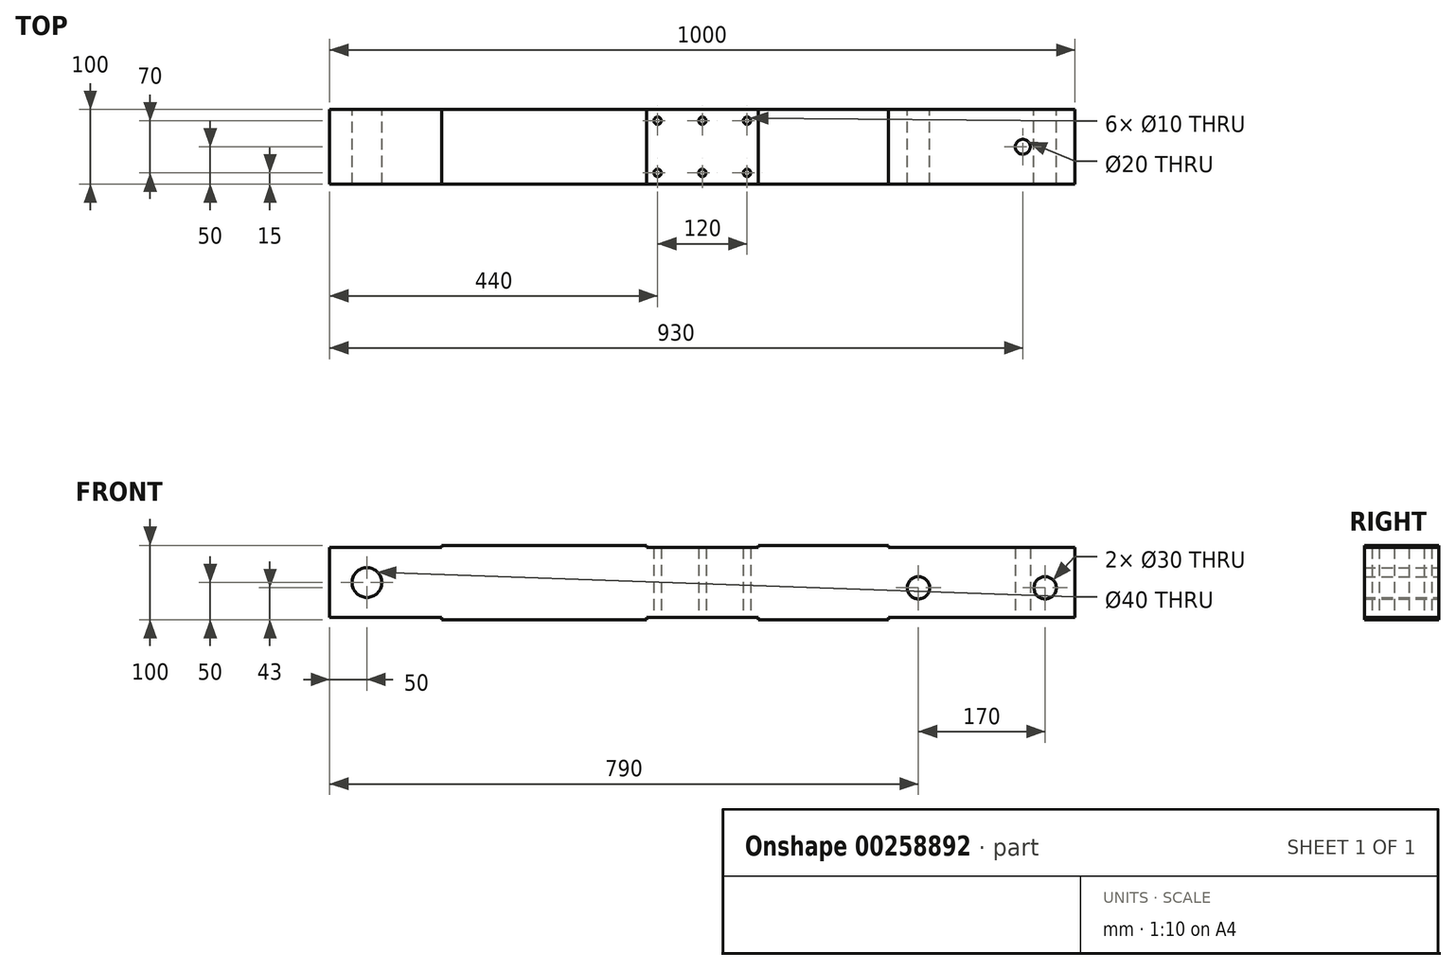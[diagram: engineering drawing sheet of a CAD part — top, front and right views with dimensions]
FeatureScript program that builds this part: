
annotation { "Feature Type Name" : "Feature", "Feature Type Description" : "" }
export const myFeature = defineFeature(function(context is Context, id is Id, definition is map)
    precondition{}
    {
        {
            var Q0;
            Q0=qCreatedBy(makeId("Top.planeOp"),FACE);
            var sketch = newSketch(context, id + "F0", { "sketchPlane" : qUnion([Q0])});
            skLineSegment(sketch, "E0.bottom", {"start": v(-75, 50) * mm, "end": v(75, 50) * mm});
            skLineSegment(sketch, "E0.top", {"start": v(-75, -50) * mm, "end": v(75, -50) * mm});
            skLineSegment(sketch, "E0.left", {"start": v(-75, 50) * mm, "end": v(-75, -50) * mm, "construction": true});
            skLineSegment(sketch, "E0.right", {"start": v(75, 50) * mm, "end": v(75, -50) * mm, "construction": true});
            skPoint(sketch, "E0.middle", {"position": v(0, 0) * mm});
            skLineSegment(sketch, "E1.bottom", {"start": v(-500, 50) * mm, "end": v(500, 50) * mm});
            skLineSegment(sketch, "E1.top", {"start": v(-500, -50) * mm, "end": v(500, -50) * mm});
            skLineSegment(sketch, "E1.left", {"start": v(-500, 50) * mm, "end": v(-500, -50) * mm});
            skLineSegment(sketch, "E1.right", {"start": v(500, 50) * mm, "end": v(500, -50) * mm});
            skLineSegment(sketch, "E2.bottom", {"start": v(-60, 35) * mm, "end": v(60, 35) * mm, "construction": true});
            skLineSegment(sketch, "E2.top", {"start": v(-60, -35) * mm, "end": v(60, -35) * mm, "construction": true});
            skLineSegment(sketch, "E2.left", {"start": v(-60, 35) * mm, "end": v(-60, -35) * mm, "construction": true});
            skLineSegment(sketch, "E2.right", {"start": v(60, 35) * mm, "end": v(60, -35) * mm, "construction": true});
            skCircle(sketch, "E3", {"center": v(-60, 35) * mm, "radius": 5 * mm});
            skCircle(sketch, "E4", {"center": v(-60, -35) * mm, "radius": 5 * mm});
            skCircle(sketch, "E5", {"center": v(0, -35) * mm, "radius": 5 * mm});
            skCircle(sketch, "E6", {"center": v(60, -35) * mm, "radius": 5 * mm});
            skCircle(sketch, "E7", {"center": v(60, 35) * mm, "radius": 5 * mm});
            skCircle(sketch, "E8", {"center": v(0, 35) * mm, "radius": 5 * mm});
            skLineSegment(sketch, "E9", {"start": v(430, 50) * mm, "end": v(430, 0) * mm, "construction": true});
            skLineSegment(sketch, "E10", {"start": v(430, 0) * mm, "end": v(430, -50) * mm, "construction": true});
            skLineSegment(sketch, "E11", {"start": v(430, 0) * mm, "end": v(500, 0) * mm, "construction": true});
            skCircle(sketch, "E12", {"center": v(430, 0) * mm, "radius": 10 * mm});
            skSolve(sketch);
        }
        {
            var Q0;
            Q0=qCreatedBy(makeId("Front.planeOp"),FACE);
            var sketch = newSketch(context, id + "F1", { "sketchPlane" : qUnion([Q0])});
            skLineSegment(sketch, "E13.bottom", {"start": v(-75, 47) * mm, "end": v(75, 47) * mm});
            skLineSegment(sketch, "E13.top", {"start": v(-75, -47) * mm, "end": v(75, -47) * mm});
            skLineSegment(sketch, "E13.left", {"start": v(-75, 47) * mm, "end": v(-75, -47) * mm, "construction": true});
            skLineSegment(sketch, "E13.right", {"start": v(75, 47) * mm, "end": v(75, -47) * mm, "construction": true});
            skPoint(sketch, "E13.middle", {"position": v(0, 0) * mm});
            skLineSegment(sketch, "E14", {"start": v(-75, 47) * mm, "end": v(-75, 50) * mm});
            skLineSegment(sketch, "E15", {"start": v(-75, 50) * mm, "end": v(-350, 50) * mm});
            skLineSegment(sketch, "E16", {"start": v(-350, -50) * mm, "end": v(-75, -50) * mm});
            skLineSegment(sketch, "E17", {"start": v(-75, -50) * mm, "end": v(-75, -47) * mm});
            skLineSegment(sketch, "E18", {"start": v(75, -47) * mm, "end": v(75, -50) * mm});
            skLineSegment(sketch, "E19", {"start": v(75, -50) * mm, "end": v(250, -50) * mm});
            skLineSegment(sketch, "E20", {"start": v(250, 50) * mm, "end": v(75, 50) * mm});
            skLineSegment(sketch, "E21", {"start": v(75, 50) * mm, "end": v(75, 47) * mm});
            skLineSegment(sketch, "E22", {"start": v(250, 50) * mm, "end": v(250, 47) * mm});
            skLineSegment(sketch, "E23", {"start": v(250, 47) * mm, "end": v(250, -47) * mm, "construction": true});
            skLineSegment(sketch, "E24", {"start": v(250, -47) * mm, "end": v(250, -50) * mm});
            skLineSegment(sketch, "E25", {"start": v(-350, 50) * mm, "end": v(-350, 47) * mm});
            skLineSegment(sketch, "E26", {"start": v(-350, 47) * mm, "end": v(-350, -47) * mm, "construction": true});
            skLineSegment(sketch, "E27", {"start": v(-350, -47) * mm, "end": v(-350, -50) * mm});
            skLineSegment(sketch, "E28", {"start": v(-350, 47) * mm, "end": v(-500, 47) * mm});
            skLineSegment(sketch, "E29", {"start": v(-500, 47) * mm, "end": v(-500, -47) * mm});
            skLineSegment(sketch, "E30", {"start": v(-500, -47) * mm, "end": v(-350, -47) * mm});
            skLineSegment(sketch, "E31", {"start": v(250, 47) * mm, "end": v(500, 47) * mm});
            skLineSegment(sketch, "E32", {"start": v(500, 47) * mm, "end": v(500, -47) * mm});
            skLineSegment(sketch, "E33", {"start": v(500, -47) * mm, "end": v(250, -47) * mm});
            skLineSegment(sketch, "E34", {"start": v(250, 33) * mm, "end": v(500, 33) * mm, "construction": true});
            skLineSegment(sketch, "E35", {"start": v(290, 33) * mm, "end": v(290, -7) * mm, "construction": true});
            skLineSegment(sketch, "E36", {"start": v(290, -7) * mm, "end": v(250, -7) * mm, "construction": true});
            skLineSegment(sketch, "E37", {"start": v(290, -7) * mm, "end": v(290, -47) * mm, "construction": true});
            skLineSegment(sketch, "E38", {"start": v(460, -47) * mm, "end": v(460, -7) * mm, "construction": true});
            skLineSegment(sketch, "E39", {"start": v(460, -7) * mm, "end": v(500, -7) * mm, "construction": true});
            skLineSegment(sketch, "E40", {"start": v(460, -7) * mm, "end": v(460, 33) * mm, "construction": true});
            skCircle(sketch, "E41", {"center": v(290, -7) * mm, "radius": 15 * mm});
            skCircle(sketch, "E42", {"center": v(460, -7) * mm, "radius": 15 * mm});
            skCircle(sketch, "E43", {"center": v(-450, 0) * mm, "radius": 20 * mm});
            skSolve(sketch);
        }
        {
            var Q0;
            {var subQ1=sQuery(id+"F0.wireOp",EDGE,"E1.left");Q0=makeQuery(id+"F0.imprint","IMPRINT",FACE,{"disambiguationData":[TD([[makeQuery(id+"F0.imprint","IMPRINT",EDGE,{"derivedFrom":subQ1}),1.0]])]});}
            extrude(context, id + "F2", {"entities" : qUnion([Q0]), "depth" : 200 * mm, "symmetric" : true});
        }
        {
            var Q0;
            Q0 = qSketchRegion(id + "F1", true);
            extrude(context, id + "F3", {"entities" : qUnion([Q0]), "operationType" : NewBodyOperationType.INTERSECT, "depth" : 100 * mm, "symmetric" : true});
        }
    });
